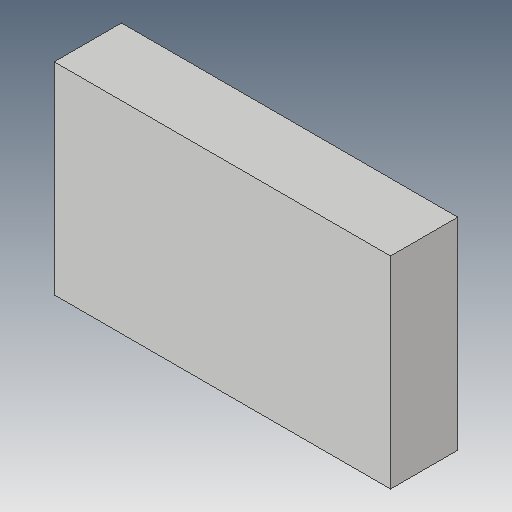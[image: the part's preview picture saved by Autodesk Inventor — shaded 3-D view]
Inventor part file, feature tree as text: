
AUTODESK INVENTOR PART (.ipt)
format: ipt  version: 2018 (Build 220112000, 112)  size: 81,920 bytes
history: native  units: in
note: dims shown in document units (in); Inventor stores cm internally (conversion verified against a paired STEP export)
features: extrude x1, sketch x1
ambient origin geometry x8: Origin, YZ Plane, XZ Plane, XY Plane, X Axis, Y Axis, Z Axis, Center Point
bodies: Solid1 (feature_tree)
feature tree (2):
  extrude  "Extrusion1"  Depth=3.0in
  sketch  "Sketch1"  dims[d0=1.0in d1=3.0in d2=5.0in d3=0.0in]
